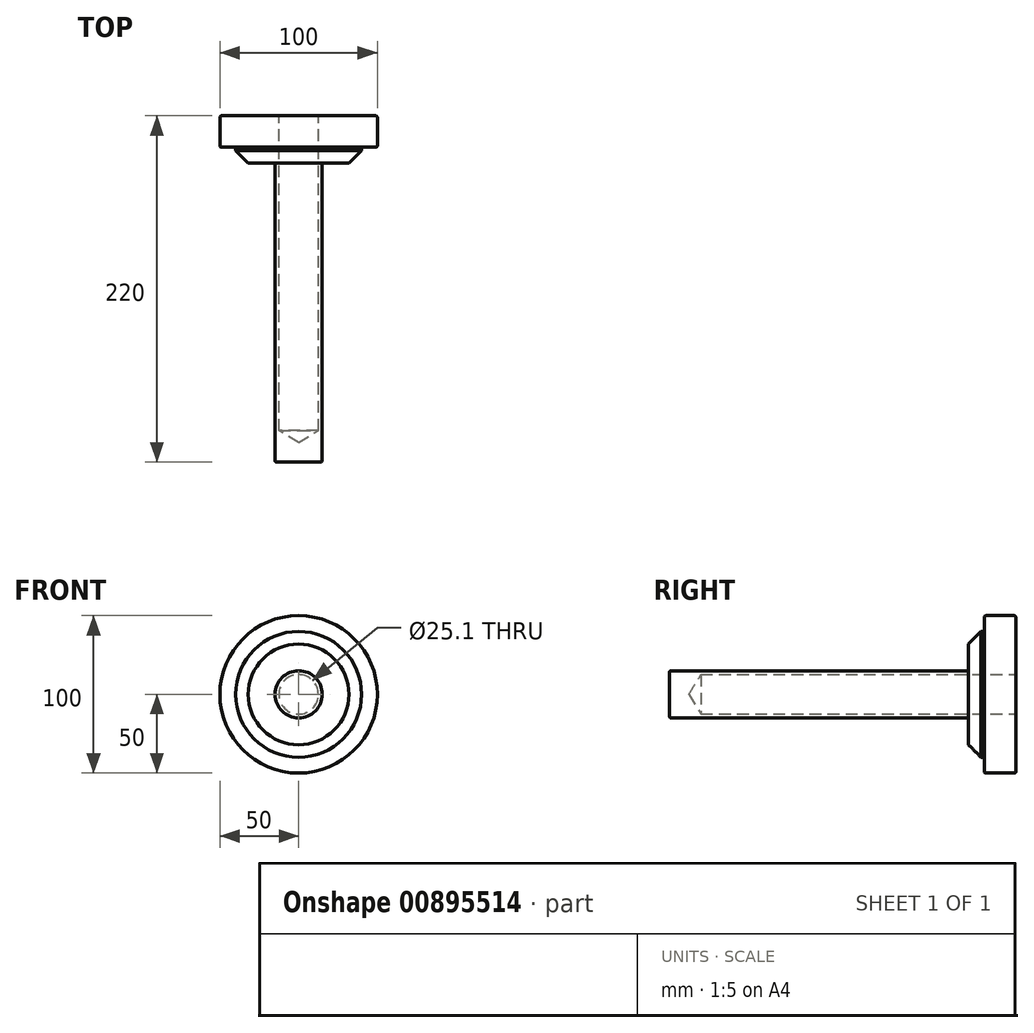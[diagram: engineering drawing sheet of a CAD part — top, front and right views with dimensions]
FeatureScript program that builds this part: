
annotation { "Feature Type Name" : "Feature", "Feature Type Description" : "" }
export const myFeature = defineFeature(function(context is Context, id is Id, definition is map)
    precondition{}
    {
        {
            var Q0;
            Q0=qCreatedBy(makeId("Top.planeOp"),FACE);
            var sketch = newSketch(context, id + "F0", { "sketchPlane" : qUnion([Q0])});
            skLineSegment(sketch, "E0", {"start": v(-15, -132.08) * mm, "end": v(15, -132.08) * mm});
            skLineSegment(sketch, "E1", {"start": v(15, -132.08) * mm, "end": v(15, 67.92) * mm});
            skLineSegment(sketch, "E2", {"start": v(15, 67.92) * mm, "end": v(50, 67.92) * mm});
            skLineSegment(sketch, "E3", {"start": v(50, 67.92) * mm, "end": v(50, 87.92) * mm});
            skLineSegment(sketch, "E4", {"start": v(50, 87.92) * mm, "end": v(-50, 87.92) * mm});
            skLineSegment(sketch, "E5", {"start": v(-50, 87.92) * mm, "end": v(-50, 67.92) * mm});
            skLineSegment(sketch, "E6", {"start": v(-50, 67.92) * mm, "end": v(-15, 67.92) * mm});
            skLineSegment(sketch, "E7", {"start": v(-15, 67.92) * mm, "end": v(-15, -132.08) * mm});
            skLineSegment(sketch, "E8", {"start": v(0, 87.92) * mm, "end": v(0, -132.08) * mm});
            skLineSegment(sketch, "E9", {"start": v(40, 67.92) * mm, "end": v(40, 57.92) * mm});
            skLineSegment(sketch, "E10", {"start": v(40, 57.92) * mm, "end": v(15, 57.92) * mm});
            skSolve(sketch);
        }
        {
            var Q0;
            {var subQ4=sQuery(id+"F0.wireOp",EDGE,"E9");Q0=makeQuery(id+"F0.imprint","IMPRINT",FACE,{"disambiguationData":[TD([[makeQuery(id+"F0.imprint","IMPRINT",EDGE,{"derivedFrom":subQ4}),-1.0]])]});}
            var Q1;
            {var subQ8=sQuery(id+"F0.wireOp",EDGE,"E3");Q1=makeQuery(id+"F0.imprint","IMPRINT",FACE,{"disambiguationData":[TD([[makeQuery(id+"F0.imprint","IMPRINT",EDGE,{"derivedFrom":subQ8}),1.0]])]});}
            var Q2;
            Q2=sQuery(id+"F0.wireOp",EDGE,"E8");
            revolve(context, id + "F1", {"surfaceOperationType" : NewSurfaceOperationType.NEW, "entities" : qUnion([Q0, Q1]), "axis" : qUnion([Q2]), "revolveType" : RevolveType.FULL});
        }
        {
            var Q0;
            Q0=makeQuery(id+"F1.opRevolve","SWEPT_FACE",FACE,{"disambiguationData":[OSD([sQuery(id+"F0.wireOp",EDGE,"E4")])]});
            var sketch = newSketch(context, id + "F2", { "sketchPlane" : qUnion([Q0])});
            skLineSegment(sketch, "E11", {"start": v(0, 0) * mm, "end": v(-50, 0) * mm});
            skPoint(sketch, "E12", {"position": v(0, 0) * mm});
            skSolve(sketch);
        }
        {
            var Q0;
            Q0=sQuery(id+"F2.wireOp",VERTEX,"E12");
            var Q1;
            Q1=makeQuery(id+"F1.opRevolve","SWEPT_BODY",BODY,{"disambiguationData":[OSD([sQuery(id+"F0.wireOp",EDGE,"E0"),sQuery(id+"F0.wireOp",EDGE,"E1"),sQuery(id+"F0.wireOp",EDGE,"E2"),sQuery(id+"F0.wireOp",EDGE,"E3"),sQuery(id+"F0.wireOp",EDGE,"E4"),sQuery(id+"F0.wireOp",EDGE,"E8")])]});
            hole(context, id + "F3", {"style" : HoleStyle.SIMPLE, "endStyle" : HoleEndStyle.BLIND, "holeDiameter" : 25.1 * mm, "majorDiameter" : 5 * mm, "holeDepth" : 200 * mm, "isTappedThrough" : true, "tappedDepth" : 12 * mm, "tapClearance" : 3, "startFromSketch" : true, "locations" : qUnion([Q0]), "scope" : qUnion([Q1])});
        }
        {
            var Q0;
            Q0=makeQuery(id+"F1.opRevolve","SWEPT_EDGE",EDGE,{"disambiguationData":[OSD([sQuery(id+"F0.wireOp",EDGE,"E3"),sQuery(id+"F0.wireOp",EDGE,"E4")])]});
            var Q1;
            Q1=makeQuery(id+"F1.opRevolve","SWEPT_EDGE",EDGE,{"disambiguationData":[OSD([sQuery(id+"F0.wireOp",EDGE,"E0"),sQuery(id+"F0.wireOp",EDGE,"E1")])]});
            fillet(context, id + "F4", {"entities" : qUnion([Q0, Q1]), "radius" : 1 * mm, "tangentPropagation" : true, "allowEdgeOverflow" : false});
        }
        {
            var Q0;
            Q0=makeQuery(id+"F1.opRevolve","SWEPT_EDGE",EDGE,{"disambiguationData":[OSD([sQuery(id+"F0.wireOp",EDGE,"E9"),sQuery(id+"F0.wireOp",EDGE,"E10")])]});
            chamfer(context, id + "F5", {"entities" : qUnion([Q0]), "width" : 8 * mm, "tangentPropagation" : true});
        }
        {
            var Q0;
            Q0=makeQuery(id+"F1.opRevolve","SWEPT_EDGE",EDGE,{"disambiguationData":[OSD([sQuery(id+"F0.wireOp",EDGE,"E2"),sQuery(id+"F0.wireOp",EDGE,"E3")])]});
            fillet(context, id + "F6", {"entities" : qUnion([Q0]), "radius" : 1 * mm, "tangentPropagation" : true, "allowEdgeOverflow" : false});
        }
    });
